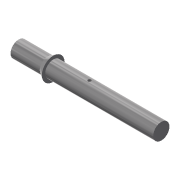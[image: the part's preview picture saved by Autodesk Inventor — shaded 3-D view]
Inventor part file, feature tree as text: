
AUTODESK INVENTOR PART (.ipt)
format: ipt  version: 2016 (Build 200138000, 138)  size: 177,152 bytes
history: native  units: mm
features: other x5, chamfer x2, sketch x2, revolve x1, extrude x1, projected_geometry x1
ambient origin geometry x6: Origin, XZ Plane, XY Plane, X Axis, Y Axis, Z Axis
bodies: Body1 (feature_tree)
feature tree (12):
  other  "Sólido1"
  revolve  "Revolución1"  [1 undecoded]
  chamfer  "Chaflán3"  [1 undecoded]
  chamfer  "Chaflán4"  Distance=3.0mm
  other  "Acanalado de llave1"
  extrude  "Extrusión1"  Depth=33.6mm
  other  "Plano inicial"
  other  "Punto de origen"
  sketch  "Boceto principal"  dims[d4=15.0mm d5=0.0mm d14=3.0mm d15=33.6mm d16=40.0mm d17=0.0mm d18=12.0mm d19=0.5mm d20=0.125mm d21=45.0deg d22=0.5mm d23=0.125mm d24=45.0deg]
  sketch  "Boceto3"  dims[d0=0.0mm d1=0.0mm d2=0.0mm d3=15.0mm]
  projected_geometry  "Contorno proyectado1"
  other  "iFeature7:1"
note: 2 required parameter values undecoded (feature->parameter linkage not recoverable at this tier; creation-order binding heuristic only, values carry confidence <= 0.55)